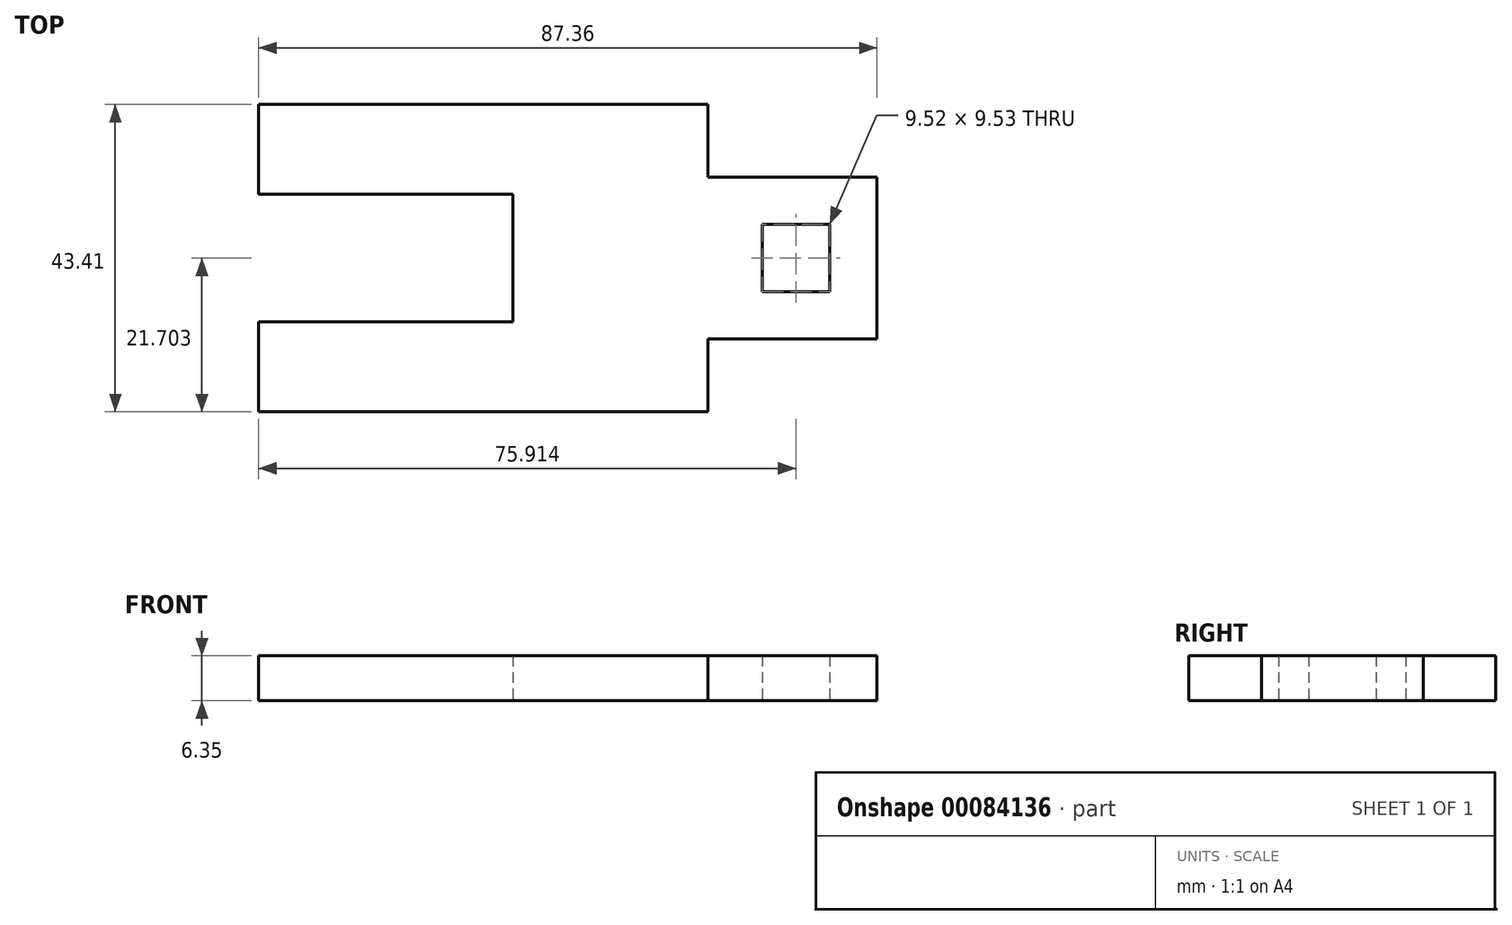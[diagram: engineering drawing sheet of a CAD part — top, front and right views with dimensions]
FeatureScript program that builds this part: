
annotation { "Feature Type Name" : "Feature", "Feature Type Description" : "" }
export const myFeature = defineFeature(function(context is Context, id is Id, definition is map)
    precondition{}
    {
        {
            var Q0;
            Q0=qCreatedBy(makeId("Top.planeOp"),FACE);
            var sketch = newSketch(context, id + "F0", { "sketchPlane" : qUnion([Q0])});
            skLineSegment(sketch, "E0", {"start": v(-62.33, 13.77) * mm, "end": v(-62.33, 26.47) * mm});
            skLineSegment(sketch, "E1", {"start": v(-62.33, 26.47) * mm, "end": v(1.17, 26.47) * mm});
            skLineSegment(sketch, "E2", {"start": v(1.17, 26.47) * mm, "end": v(1.17, 16.2) * mm});
            skLineSegment(sketch, "E3", {"start": v(1.17, 16.2) * mm, "end": v(25.03, 16.2) * mm});
            skLineSegment(sketch, "E4", {"start": v(25.03, 16.2) * mm, "end": v(25.03, -6.65) * mm});
            skLineSegment(sketch, "E5", {"start": v(25.03, -6.65) * mm, "end": v(1.17, -6.65) * mm});
            skLineSegment(sketch, "E6", {"start": v(1.17, -6.65) * mm, "end": v(1.17, -16.94) * mm});
            skLineSegment(sketch, "E7", {"start": v(1.17, -16.94) * mm, "end": v(-62.33, -16.94) * mm});
            skLineSegment(sketch, "E8", {"start": v(-62.33, -16.94) * mm, "end": v(-62.33, -4.24) * mm});
            skLineSegment(sketch, "E9", {"start": v(-62.33, -4.24) * mm, "end": v(-26.4, -4.24) * mm});
            skLineSegment(sketch, "E10", {"start": v(-26.4, -4.24) * mm, "end": v(-26.4, 13.77) * mm});
            skLineSegment(sketch, "E11", {"start": v(-26.4, 13.77) * mm, "end": v(-62.33, 13.77) * mm});
            skLineSegment(sketch, "E12.bottom", {"start": v(8.82, 9.53) * mm, "end": v(18.35, 9.53) * mm});
            skLineSegment(sketch, "E12.top", {"start": v(8.82, 0) * mm, "end": v(18.35, 0) * mm});
            skLineSegment(sketch, "E12.left", {"start": v(8.82, 9.53) * mm, "end": v(8.82, 0) * mm});
            skLineSegment(sketch, "E12.right", {"start": v(18.35, 9.53) * mm, "end": v(18.35, 0) * mm});
            skSolve(sketch);
        }
        {
            var Q0;
            Q0=makeQuery(id+"F0.imprint","IMPRINT",FACE,{"disambiguationData":[TD([[makeQuery(id+"F0.imprint","IMPRINT",EDGE,{"derivedFrom":sQuery(id+"F0.wireOp",EDGE,"E0")}),-1.0]])]});
            extrude(context, id + "F1", {"entities" : qUnion([Q0]), "depth" : 6.35 * mm});
        }
    });
